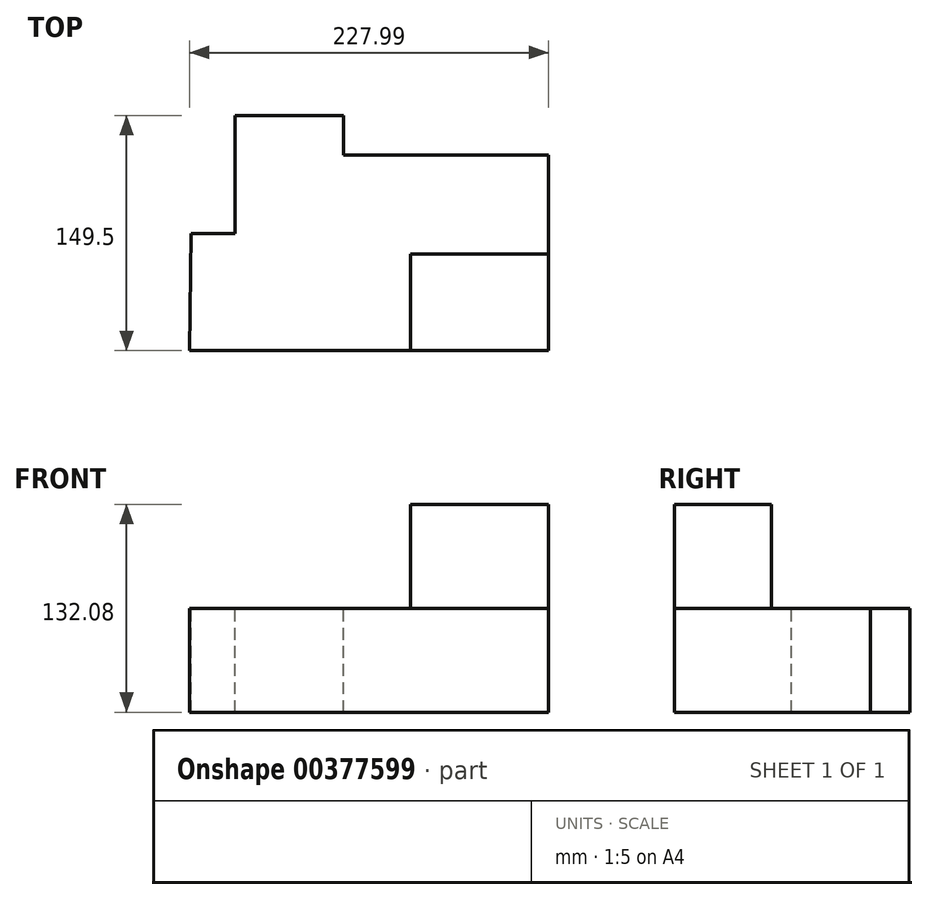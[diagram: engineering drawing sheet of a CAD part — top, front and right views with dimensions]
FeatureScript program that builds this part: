
annotation { "Feature Type Name" : "Feature", "Feature Type Description" : "" }
export const myFeature = defineFeature(function(context is Context, id is Id, definition is map)
    precondition{}
    {
        {
            var Q0;
            Q0=qCreatedBy(makeId("Top.planeOp"),FACE);
            var sketch = newSketch(context, id + "F0", { "sketchPlane" : qUnion([Q0])});
            skLineSegment(sketch, "E0", {"start": v(-97.71, -95.43) * mm, "end": v(130.28, -95.43) * mm});
            skLineSegment(sketch, "E1", {"start": v(130.28, -95.43) * mm, "end": v(130.28, 28.84) * mm});
            skLineSegment(sketch, "E2", {"start": v(130.28, 28.84) * mm, "end": v(0, 28.84) * mm});
            skLineSegment(sketch, "E3", {"start": v(0, 28.84) * mm, "end": v(0, 53.94) * mm});
            skLineSegment(sketch, "E4", {"start": v(0, 53.94) * mm, "end": v(-68.88, 53.94) * mm});
            skLineSegment(sketch, "E5", {"start": v(-68.88, 53.94) * mm, "end": v(-68.88, -21.16) * mm});
            skLineSegment(sketch, "E6", {"start": v(-68.88, -21.16) * mm, "end": v(-96.68, -21.16) * mm});
            skLineSegment(sketch, "E7", {"start": v(-96.68, -21.16) * mm, "end": v(-97.71, -95.43) * mm});
            skLineSegment(sketch, "E8", {"start": v(0, -21.16) * mm, "end": v(-68.88, -21.16) * mm});
            skLineSegment(sketch, "E9", {"start": v(0, -95.43) * mm, "end": v(0, -21.16) * mm});
            skLineSegment(sketch, "E10", {"start": v(130.28, -33.3) * mm, "end": v(42.32, -33.3) * mm});
            skLineSegment(sketch, "E11", {"start": v(42.32, -33.3) * mm, "end": v(42.32, -95.43) * mm});
            skLineSegment(sketch, "E12", {"start": v(0, -32.16) * mm, "end": v(20.12, -32.16) * mm});
            skLineSegment(sketch, "E13", {"start": v(20.12, -32.16) * mm, "end": v(20.12, -95.43) * mm});
            skPoint(sketch, "E13.endSnap0", {"position": v(16.29, -95.43) * mm});
            skSolve(sketch);
        }
        {
            var Q0;
            Q0 = qSketchRegion(id + "F0", true);
            extrude(context, id + "F1", {"entities" : qUnion([Q0]), "oppositeDirection" : true, "depth" : 66.04 * mm});
        }
        {
            var Q0;
            Q0 = qSketchRegion(id + "F0", true);
            var sketch = newSketch(context, id + "F2", { "sketchPlane" : qUnion([Q0])});
            skLineSegment(sketch, "E14", {"start": v(130.2, -95.56) * mm, "end": v(130.2, -34.02) * mm});
            skLineSegment(sketch, "E15", {"start": v(130.2, -34.02) * mm, "end": v(42.47, -34.02) * mm});
            skLineSegment(sketch, "E16", {"start": v(42.47, -34.02) * mm, "end": v(42.47, -95.56) * mm});
            skLineSegment(sketch, "E17", {"start": v(42.47, -95.56) * mm, "end": v(130.2, -95.56) * mm});
            skSolve(sketch);
        }
        {
            var Q0;
            Q0 = qSketchRegion(id + "F2", true);
            extrude(context, id + "F3", {"entities" : qUnion([Q0]), "operationType" : NewBodyOperationType.ADD, "depth" : 66.04 * mm});
        }
    });
